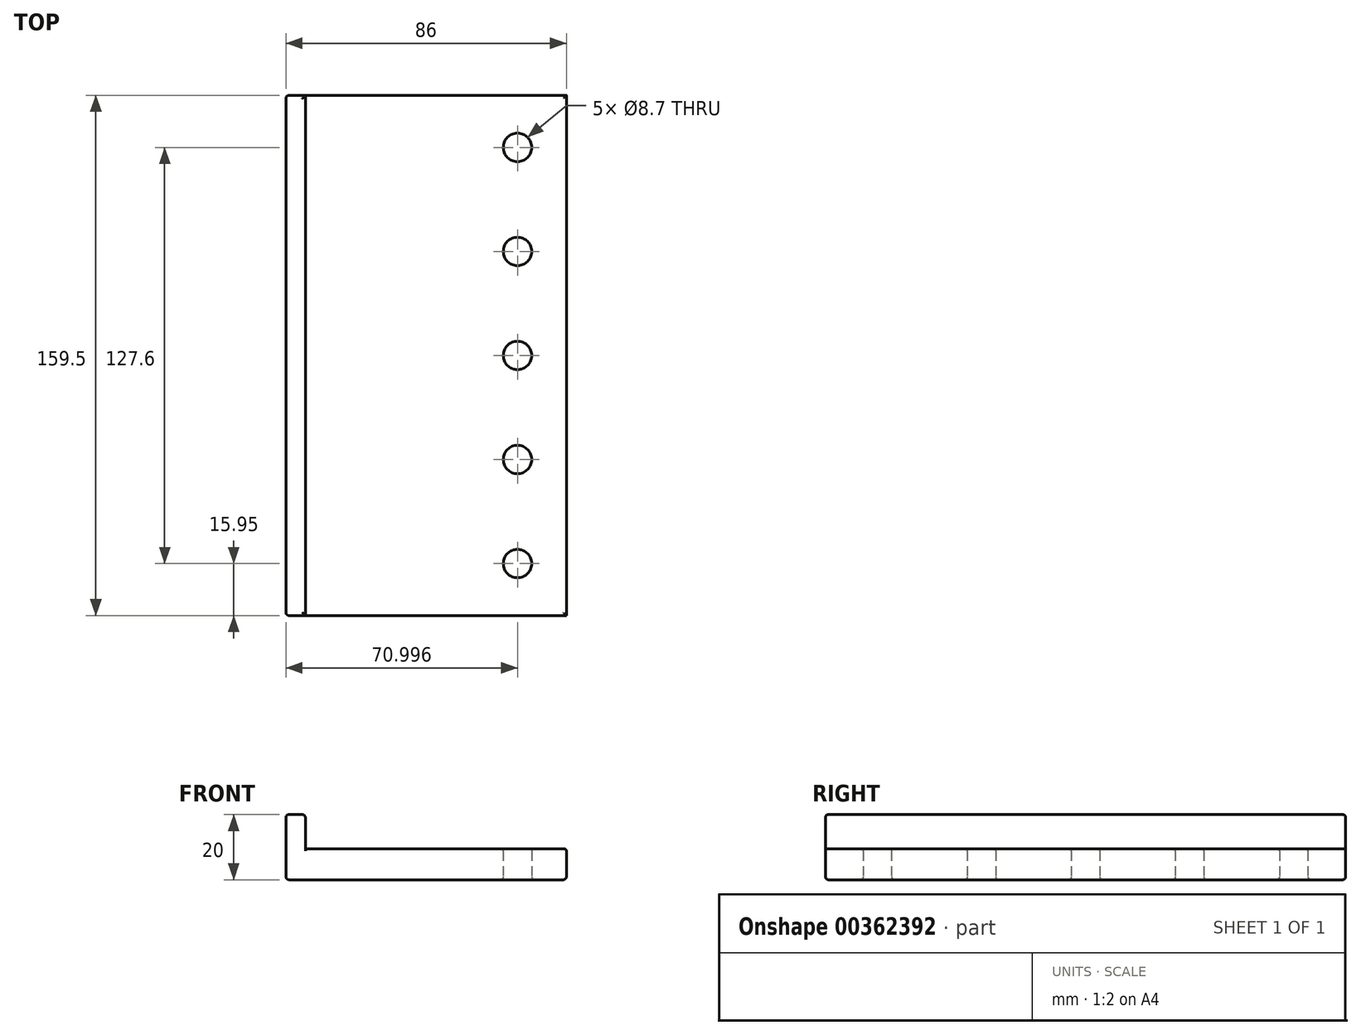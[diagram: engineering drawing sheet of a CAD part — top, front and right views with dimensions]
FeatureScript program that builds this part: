
annotation { "Feature Type Name" : "Feature", "Feature Type Description" : "" }
export const myFeature = defineFeature(function(context is Context, id is Id, definition is map)
    precondition{}
    {
        {
            var Q0;
            Q0=qCreatedBy(makeId("Top.planeOp"),FACE);
            var sketch = newSketch(context, id + "F0", { "sketchPlane" : qUnion([Q0])});
            skLineSegment(sketch, "E0.bottom", {"start": v(-38.73, 79.75) * mm, "end": v(41.27, 79.75) * mm});
            skLineSegment(sketch, "E0.top", {"start": v(-38.73, -79.75) * mm, "end": v(41.27, -79.75) * mm});
            skLineSegment(sketch, "E0.left", {"start": v(-38.73, 79.75) * mm, "end": v(-38.73, -79.75) * mm});
            skLineSegment(sketch, "E0.right", {"start": v(41.27, 79.75) * mm, "end": v(41.27, -79.75) * mm});
            skPoint(sketch, "E1", {"position": v(-38.73, 0) * mm});
            skLineSegment(sketch, "E2", {"start": v(26.27, 79.75) * mm, "end": v(26.27, -79.75) * mm, "construction": true});
            skCircle(sketch, "E3", {"center": v(26.27, 63.8) * mm, "radius": 4.35 * mm});
            skCircle(sketch, "E4", {"center": v(26.27, 31.9) * mm, "radius": 4.35 * mm});
            skCircle(sketch, "E5", {"center": v(26.27, 0) * mm, "radius": 4.35 * mm});
            skCircle(sketch, "E6", {"center": v(26.27, -31.9) * mm, "radius": 4.35 * mm});
            skCircle(sketch, "E7", {"center": v(26.27, -63.8) * mm, "radius": 4.35 * mm});
            skSolve(sketch);
        }
        {
            var Q0;
            Q0=makeQuery(id+"F0.imprint","IMPRINT",FACE,{"disambiguationData":[TD([[makeQuery(id+"F0.imprint","IMPRINT",EDGE,{"derivedFrom":sQuery(id+"F0.wireOp",EDGE,"E0.bottom")}),-1.0]])]});
            extrude(context, id + "F1", {"entities" : qUnion([Q0]), "depth" : 9.5 * mm});
        }
        {
            var Q0;
            Q0=qCreatedBy(makeId("Top.planeOp"),FACE);
            var sketch = newSketch(context, id + "F2", { "sketchPlane" : qUnion([Q0])});
            skLineSegment(sketch, "E8.bottom", {"start": v(-44.73, 79.75) * mm, "end": v(-38.73, 79.75) * mm});
            skLineSegment(sketch, "E8.top", {"start": v(-44.73, -79.75) * mm, "end": v(-38.73, -79.75) * mm});
            skLineSegment(sketch, "E8.left", {"start": v(-44.73, 79.75) * mm, "end": v(-44.73, -79.75) * mm});
            skLineSegment(sketch, "E8.right", {"start": v(-38.73, 79.75) * mm, "end": v(-38.73, -79.75) * mm});
            skSolve(sketch);
        }
        {
            var Q0;
            Q0=makeQuery(id+"F2.imprint","IMPRINT",FACE,{"disambiguationData":[TD([[makeQuery(id+"F2.imprint","IMPRINT",EDGE,{"derivedFrom":sQuery(id+"F2.wireOp",EDGE,"E8.bottom")}),-1.0]])]});
            extrude(context, id + "F3", {"entities" : qUnion([Q0]), "operationType" : NewBodyOperationType.ADD, "depth" : 20 * mm});
        }
        {
            var Q0;
            Q0=makeQuery(id+"F3.opExtrude","CAP_FACE",FACE,{"disambiguationData":[OSD([sQuery(id+"F2.wireOp",EDGE,"E8.bottom"),sQuery(id+"F2.wireOp",EDGE,"E8.top"),sQuery(id+"F2.wireOp",EDGE,"E8.left"),sQuery(id+"F2.wireOp",EDGE,"E8.right")])],"isStart":false});
            var Q1;
            Q1=makeQuery(id+"F3.opExtrude","SWEPT_FACE",FACE,{"disambiguationData":[OSD([sQuery(id+"F2.wireOp",EDGE,"E8.left")])]});
            var Q2;
            Q2=makeQuery(id+"F3.boolean.opBoolean","MERGE",FACE,{"derivedFrom":[makeQuery(id+"F1.opExtrude","CAP_FACE",FACE,{"disambiguationData":[OSD([sQuery(id+"F0.wireOp",EDGE,"E0.bottom"),sQuery(id+"F0.wireOp",EDGE,"E0.top"),sQuery(id+"F0.wireOp",EDGE,"E0.left"),sQuery(id+"F0.wireOp",EDGE,"E0.right"),sQuery(id+"F0.wireOp",EDGE,"E3"),sQuery(id+"F0.wireOp",EDGE,"E4"),sQuery(id+"F0.wireOp",EDGE,"E5"),sQuery(id+"F0.wireOp",EDGE,"E6"),sQuery(id+"F0.wireOp",EDGE,"E7")])],"isStart":true}),makeQuery(id+"F3.opExtrude","CAP_FACE",FACE,{"disambiguationData":[OSD([sQuery(id+"F2.wireOp",EDGE,"E8.bottom"),sQuery(id+"F2.wireOp",EDGE,"E8.top"),sQuery(id+"F2.wireOp",EDGE,"E8.left"),sQuery(id+"F2.wireOp",EDGE,"E8.right")])],"isStart":true})]});
            fillet(context, id + "F4", {"entities" : qUnion([Q0, Q1, Q2]), "radius" : 1 * mm, "tangentPropagation" : true, "allowEdgeOverflow" : false});
        }
        {
            var Q0;
            Q0=makeQuery(id+"F1.opExtrude","CAP_EDGE",EDGE,{"disambiguationData":[OSD([sQuery(id+"F0.wireOp",EDGE,"E0.top")])],"isStart":false});
            var Q1;
            Q1=makeQuery(id+"F1.opExtrude","CAP_EDGE",EDGE,{"disambiguationData":[OSD([sQuery(id+"F0.wireOp",EDGE,"E0.right")])],"isStart":false});
            var Q2;
            Q2=makeQuery(id+"F1.opExtrude","CAP_EDGE",EDGE,{"disambiguationData":[OSD([sQuery(id+"F0.wireOp",EDGE,"E0.bottom")])],"isStart":false});
            var Q3;
            Q3=makeQuery(id+"F1.opExtrude","CAP_EDGE",EDGE,{"disambiguationData":[OSD([sQuery(id+"F0.wireOp",EDGE,"E3")])],"isStart":false});
            var Q4;
            Q4=makeQuery(id+"F1.opExtrude","CAP_EDGE",EDGE,{"disambiguationData":[OSD([sQuery(id+"F0.wireOp",EDGE,"E4")])],"isStart":false});
            var Q5;
            Q5=makeQuery(id+"F1.opExtrude","CAP_EDGE",EDGE,{"disambiguationData":[OSD([sQuery(id+"F0.wireOp",EDGE,"E5")])],"isStart":false});
            var Q6;
            Q6=makeQuery(id+"F1.opExtrude","CAP_EDGE",EDGE,{"disambiguationData":[OSD([sQuery(id+"F0.wireOp",EDGE,"E6")])],"isStart":false});
            var Q7;
            Q7=makeQuery(id+"F1.opExtrude","CAP_EDGE",EDGE,{"disambiguationData":[OSD([sQuery(id+"F0.wireOp",EDGE,"E7")])],"isStart":false});
            fillet(context, id + "F5", {"entities" : qUnion([Q0, Q1, Q2, Q3, Q4, Q5, Q6, Q7]), "radius" : .7 * mm, "tangentPropagation" : true, "allowEdgeOverflow" : false});
        }
    });
